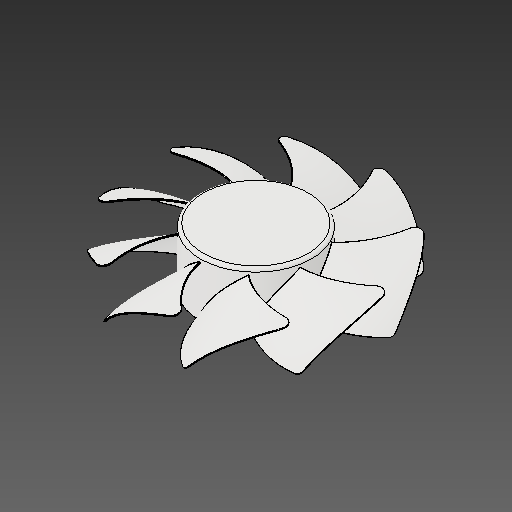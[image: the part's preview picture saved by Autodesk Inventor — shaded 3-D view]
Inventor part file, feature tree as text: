
AUTODESK INVENTOR PART (.ipt)
format: ipt  version: 2018.2 (Build 222227000, 227)  size: 1,533,952 bytes
history: native  units: mm
features: other x1, fillet x1
ambient origin geometry x8: Origin, YZ Plane, XZ Plane, XY Plane, X Axis, Y Axis, Z Axis, Center Point
bodies: Body1 (feature_tree)
feature tree (2):
  other  "ソリッド1"
  fillet  "Fillet4"  [1 undecoded]
note: 1 required parameter value undecoded (feature->parameter linkage not recoverable at this tier; creation-order binding heuristic only, values carry confidence <= 0.55)
